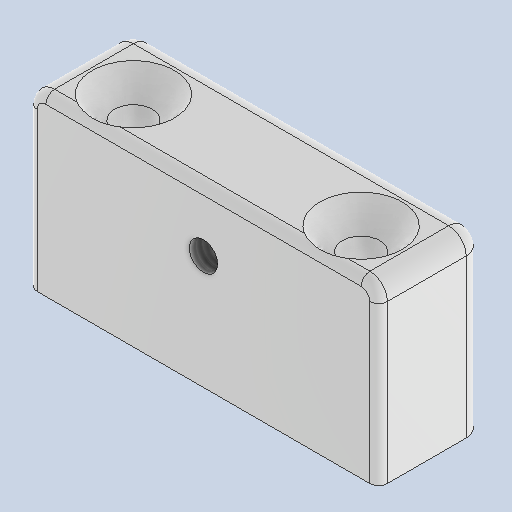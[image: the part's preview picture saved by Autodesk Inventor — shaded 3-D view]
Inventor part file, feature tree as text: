
AUTODESK INVENTOR PART (.ipt)
format: ipt  version: 2025 (Build 290162010, 162A)  size: 295,936 bytes
history: native  units: mm
features: sketch x3, hole x2, fillet x2, extrude x1
ambient origin geometry x8: Origin, YZ Plane, XZ Plane, XY Plane, X Axis, Y Axis, Z Axis, Center Point
bodies: Volumenkörper1 (feature_tree)
feature tree (8):
  extrude  "Extrusion1"  Depth=12.0mm
  hole  "Bohrung1"  [1 undecoded]
  hole  "Bohrung4"  [1 undecoded]
  fillet  "Rundung2"  Radius=7.0mm
  fillet  "Rundung3"  Radius=2.0mm
  sketch  "Skizze1"  dims[d0=40.0mm d1=12.0mm]
  sketch  "Skizze2"  dims[d2=20.0mm d3=0.0mm d4=7.0mm]
  sketch  "Skizze3"  dims[d5=4.3mm d6=6.0mm d7=9.4mm d8=4.0mm d9=90.0deg d10=15.0mm d11=20.594885mm d12=7.0mm d14=7.0mm d29=3.242mm d30=8.0mm d31=4.0mm d32=2.0mm d33=90.0deg d34=10.0mm d35=20.594885mm d36=2.0mm d37=1.0mm d38=0.0625mm d39=0.75mm d40=0.375mm]
note: 2 required parameter values undecoded (feature->parameter linkage not recoverable at this tier; creation-order binding heuristic only, values carry confidence <= 0.55)
